# Revit family: Haworth_Janus_Quinta_Chair_Cafe
name_source: partatom
category: Furniture
revit_build: Autodesk Revit 2018 (Build: 20170223_1515(x64)
units: mm (PartAtom-declared; Revit-internal decimal feet)

## family parameters
Always vertical = Yes
Cut with Voids When Loaded = No
OmniClass Number = 23.40.70.14.64.21
OmniClass Title = Systems Furniture
Room Calculation Point = No
Shared = No
Work Plane-Based = No

## types (2) — shared parameters
Actual Depth = 23 1/2"
Actual Height = 33"
Actual Width = 21 1/2"
Arm Height = 25 3/4"
Assembly Code = E2020200
Description = Haworth Janus Quinta - Cafe Side Chair with Arms
Glide Finish = Haworth _ Polymer _ Black
Manufacturer = Haworth
Model = HCJC-QN-SAC-J
Revision Number = 2
Seat Height = 18"
Size = Verify Final Dim. w/ Haworth
URL = http://www.haworth.com
URL - Product = https://www.haworth.com
Warranty = https://www.haworth.com

## per-type parameters (varying)
| type | Cushion |
| HCJC-QN-SAC-J - With Arms - Fiber Frame - With Cushion | Yes |
| HCJC-QN-SAC-J - With Arms - Fiber Frame - No Cushion | No |

## geometry (parser evidence)
native form markers: Sweep x5
no freeform markers — native parametric forms only
